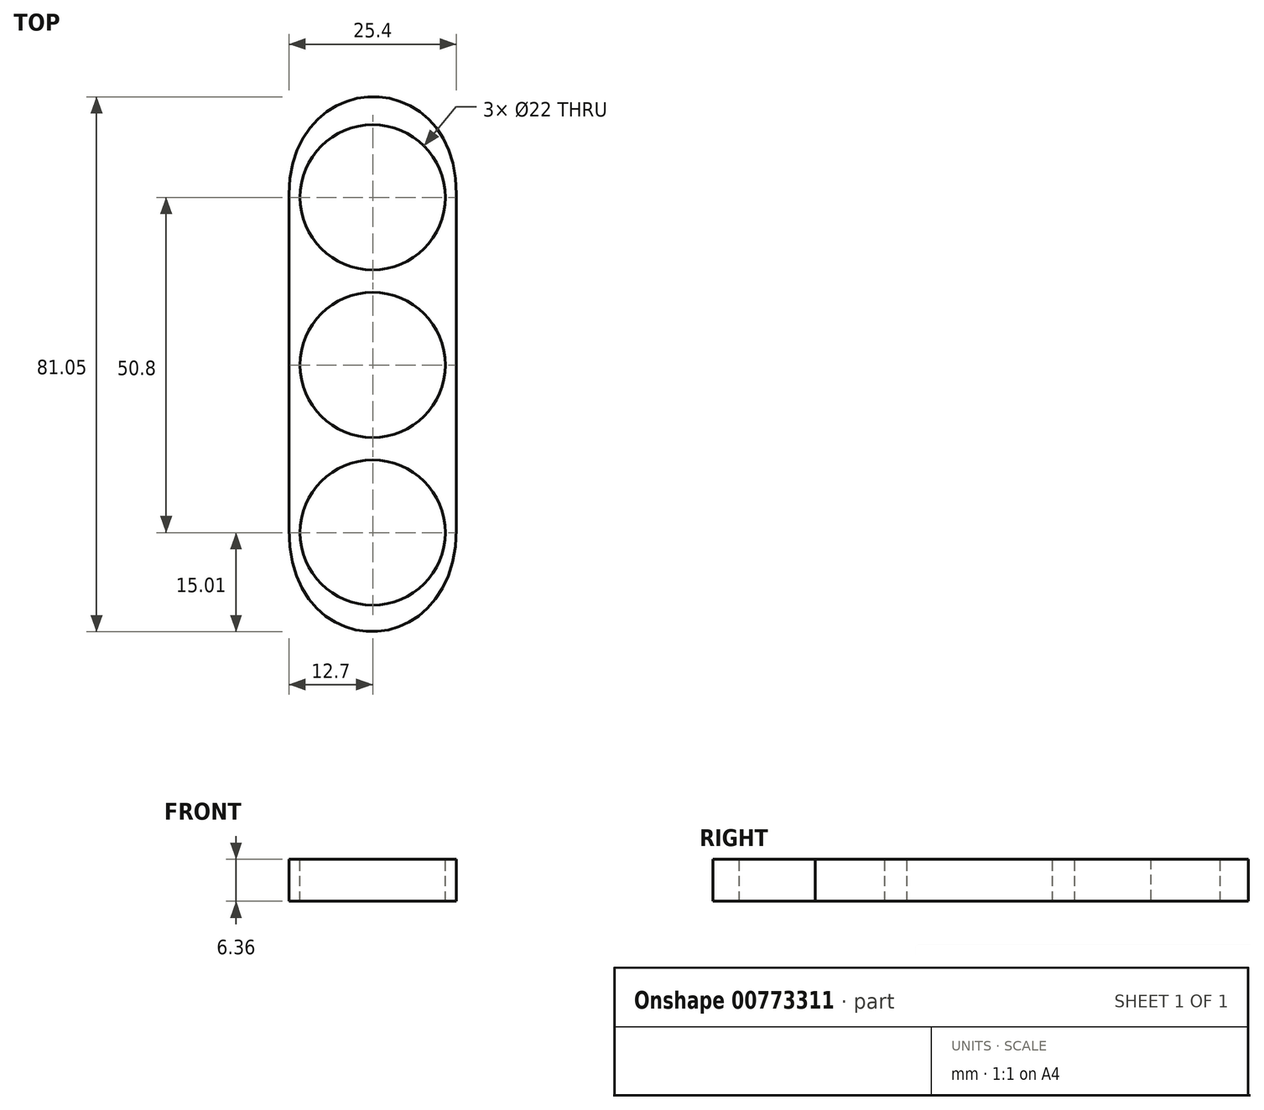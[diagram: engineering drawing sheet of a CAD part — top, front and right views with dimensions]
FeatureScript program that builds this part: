
annotation { "Feature Type Name" : "Feature", "Feature Type Description" : "" }
export const myFeature = defineFeature(function(context is Context, id is Id, definition is map)
    precondition{}
    {
        {
            var Q0;
            Q0=qCreatedBy(makeId("Top.planeOp"),FACE);
            var sketch = newSketch(context, id + "F0", { "sketchPlane" : qUnion([Q0])});
            skCircle(sketch, "E0", {"center": v(0, 0) * mm, "radius": 11 * mm});
            skCircle(sketch, "E1", {"center": v(0, 25.4) * mm, "radius": 11 * mm});
            skCircle(sketch, "E2", {"center": v(0, -25.4) * mm, "radius": 11 * mm});
            skSolve(sketch);
        }
        {
            var Q0;
            Q0=qCreatedBy(makeId("Top.planeOp"),FACE);
            var sketch = newSketch(context, id + "F1", { "sketchPlane" : qUnion([Q0])});
            skLineSegment(sketch, "E3", {"start": v(-12.7, 25.85) * mm, "end": v(-12.7, -24.95) * mm});
            skLineSegment(sketch, "E4", {"start": v(12.7, 25.86) * mm, "end": v(12.7, -24.94) * mm});
            skFitSpline(sketch, "E5", {"points": [v(-12.7, 25.85) * mm, v(12.7, 25.86) * mm], "startDerivative": vector(0.65, 59.16) * mm, "endDerivative": vector(-0.25, -59.14) * mm});
            skFitSpline(sketch, "E6", {"points": [v(-12.7, -24.95) * mm, v(12.7, -24.94) * mm], "startDerivative": vector(-0.25, -61.86) * mm, "endDerivative": vector(0.65, 61.87) * mm});
            skSolve(sketch);
        }
        {
            var Q0;
            Q0 = qSketchRegion(id + "F1", true);
            extrude(context, id + "F2", {"entities" : qUnion([Q0]), "endBound" : BoundingType.SYMMETRIC, "depth" : 6.35 * mm, "offsetDistance" : 25.4 * mm});
        }
        {
            var Q0;
            Q0 = qSketchRegion(id + "F0", true);
            extrude(context, id + "F3", {"entities" : qUnion([Q0]), "operationType" : NewBodyOperationType.REMOVE, "endBound" : BoundingType.SYMMETRIC, "oppositeDirection" : true, "depth" : 6.35 * mm, "offsetDistance" : 25.4 * mm});
        }
    });
